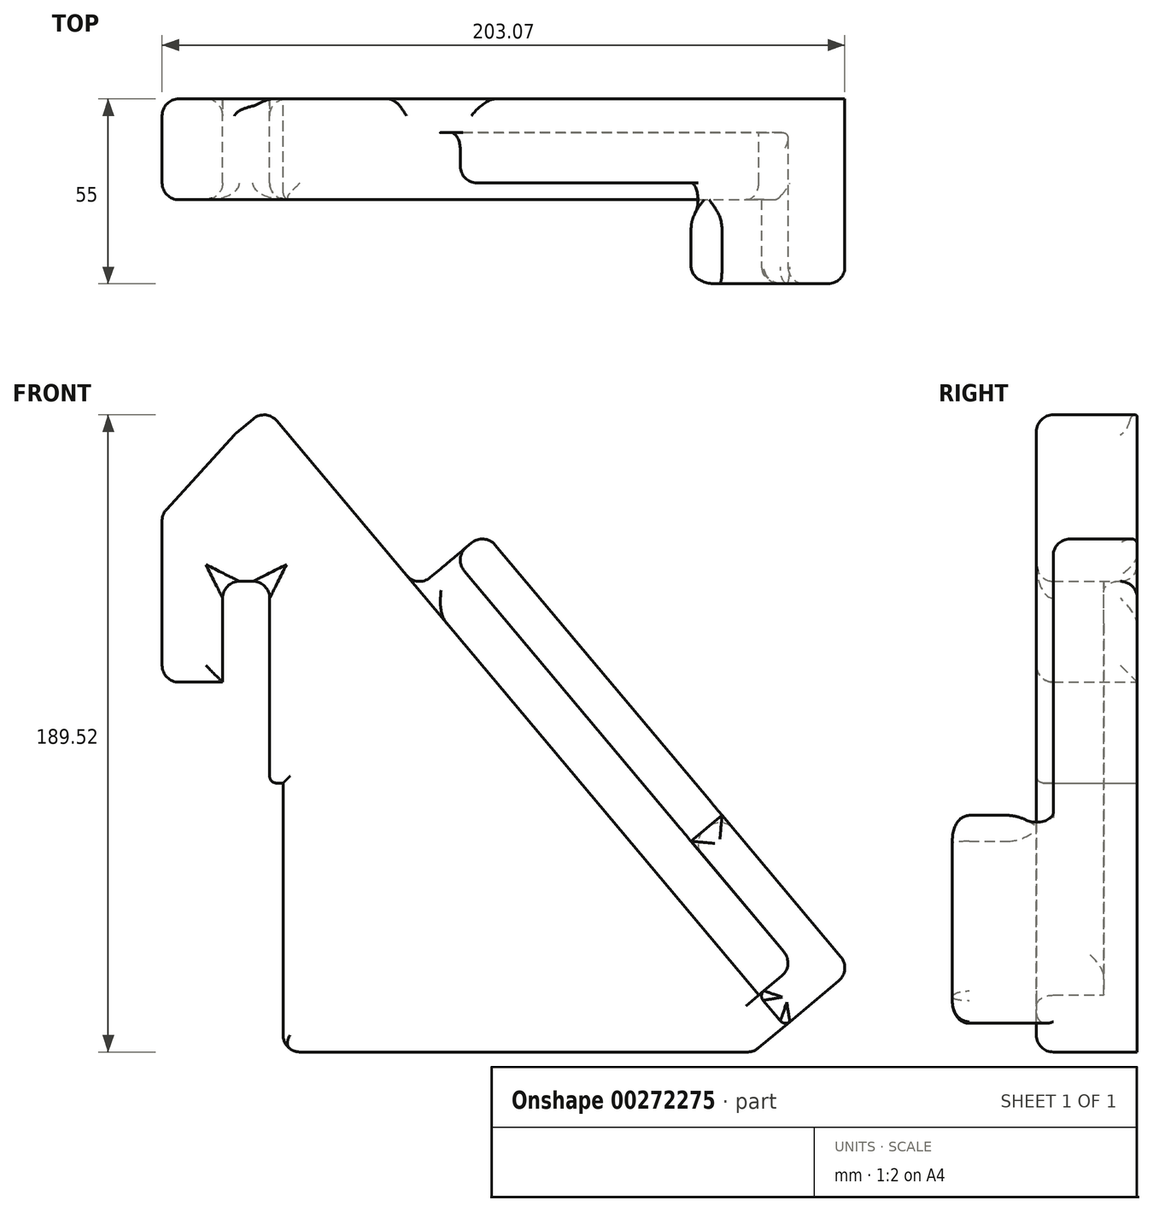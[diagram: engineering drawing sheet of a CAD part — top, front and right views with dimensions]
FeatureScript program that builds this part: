
annotation { "Feature Type Name" : "Feature", "Feature Type Description" : "" }
export const myFeature = defineFeature(function(context is Context, id is Id, definition is map)
    precondition{}
    {
        {
            var Q0;
            Q0=qCreatedBy(makeId("Front.planeOp"),FACE);
            var sketch = newSketch(context, id + "F0", { "sketchPlane" : qUnion([Q0])});
            skLineSegment(sketch, "E0", {"start": v(0, 0) * mm, "end": v(0, 50) * mm});
            skLineSegment(sketch, "E1", {"start": v(0, 50) * mm, "end": v(41.74, 50) * mm});
            skLineSegment(sketch, "E2", {"start": v(41.74, 50) * mm, "end": v(176, -110) * mm});
            skLineSegment(sketch, "E3", {"start": v(176, -110) * mm, "end": v(205.1, -85.57) * mm});
            skLineSegment(sketch, "E4", {"start": v(205.1, -85.57) * mm, "end": v(166.54, -39.61) * mm});
            skLineSegment(sketch, "E5", {"start": v(32, 0) * mm, "end": v(32, -30) * mm});
            skLineSegment(sketch, "E6", {"start": v(32, -30) * mm, "end": v(36, -30) * mm});
            skLineSegment(sketch, "E7", {"start": v(36, -30) * mm, "end": v(36, -110) * mm});
            skLineSegment(sketch, "E8", {"start": v(36, -110) * mm, "end": v(176, -110) * mm});
            skLineSegment(sketch, "E9", {"start": v(32, 0) * mm, "end": v(32, 0) * mm});
            skLineSegment(sketch, "E10", {"start": v(0, 0) * mm, "end": v(18, 0) * mm});
            skLineSegment(sketch, "E11", {"start": v(18, 0) * mm, "end": v(18, 30) * mm});
            skLineSegment(sketch, "E12", {"start": v(18, 30) * mm, "end": v(32, 30) * mm});
            skLineSegment(sketch, "E13", {"start": v(32, 30) * mm, "end": v(32, 0) * mm});
            skLineSegment(sketch, "E14", {"start": v(41.74, 50) * mm, "end": v(21.73, 73.85) * mm});
            skLineSegment(sketch, "E15", {"start": v(21.73, 73.85) * mm, "end": v(30.92, 81.56) * mm});
            skLineSegment(sketch, "E16", {"start": v(30.92, 81.56) * mm, "end": v(177.48, -93.1) * mm});
            skLineSegment(sketch, "E17", {"start": v(177.48, -93.1) * mm, "end": v(188.2, -84.1) * mm});
            skLineSegment(sketch, "E18", {"start": v(188.2, -84.1) * mm, "end": v(157.35, -47.32) * mm});
            skLineSegment(sketch, "E19", {"start": v(157.35, -47.32) * mm, "end": v(166.54, -39.61) * mm});
            skLineSegment(sketch, "E20", {"start": v(0, 50) * mm, "end": v(21.73, 73.85) * mm});
            skSolve(sketch);
        }
        {
            var Q0;
            Q0=makeQuery(id+"F0.imprint","IMPRINT",FACE,{"disambiguationData":[TD([[makeQuery(id+"F0.imprint","IMPRINT",EDGE,{"derivedFrom":sQuery(id+"F0.wireOp",EDGE,"E0")}),-1.0]])]});
            var Q1;
            Q1=makeQuery(id+"F0.imprint","IMPRINT",FACE,{"disambiguationData":[TD([[makeQuery(id+"F0.imprint","IMPRINT",EDGE,{"derivedFrom":sQuery(id+"F0.wireOp",EDGE,"E2")}),1.0]])]});
            var Q2;
            Q2=makeQuery(id+"F0.imprint","IMPRINT",FACE,{"disambiguationData":[TD([[makeQuery(id+"F0.imprint","IMPRINT",EDGE,{"derivedFrom":sQuery(id+"F0.wireOp",EDGE,"E1")}),1.0]])]});
            extrude(context, id + "F1", {"entities" : qUnion([Q0, Q1, Q2]), "depth" : 30 * mm});
        }
        {
            var Q0;
            Q0=makeQuery(id+"F1.opExtrude","CAP_FACE",FACE,{"disambiguationData":[OSD([sQuery(id+"F0.wireOp",EDGE,"E0"),sQuery(id+"F0.wireOp",EDGE,"E1"),sQuery(id+"F0.wireOp",EDGE,"E3"),sQuery(id+"F0.wireOp",EDGE,"E4"),sQuery(id+"F0.wireOp",EDGE,"E5"),sQuery(id+"F0.wireOp",EDGE,"E6"),sQuery(id+"F0.wireOp",EDGE,"E7"),sQuery(id+"F0.wireOp",EDGE,"E8"),sQuery(id+"F0.wireOp",EDGE,"E10"),sQuery(id+"F0.wireOp",EDGE,"E11"),sQuery(id+"F0.wireOp",EDGE,"E12"),sQuery(id+"F0.wireOp",EDGE,"E13"),sQuery(id+"F0.wireOp",EDGE,"E14"),sQuery(id+"F0.wireOp",EDGE,"E15"),sQuery(id+"F0.wireOp",EDGE,"E16"),sQuery(id+"F0.wireOp",EDGE,"E17"),sQuery(id+"F0.wireOp",EDGE,"E18"),sQuery(id+"F0.wireOp",EDGE,"E19")])],"isStart":true});
            var sketch = newSketch(context, id + "F2", { "sketchPlane" : qUnion([Q0])});
            skLineSegment(sketch, "E21", {"start": v(-188.2, -84.1) * mm, "end": v(-177.48, -93.1) * mm});
            skLineSegment(sketch, "E22", {"start": v(-188.2, -84.1) * mm, "end": v(-157.35, -47.32) * mm});
            skLineSegment(sketch, "E23", {"start": v(-157.35, -47.32) * mm, "end": v(-146.63, -56.32) * mm});
            skLineSegment(sketch, "E24", {"start": v(-146.63, -56.32) * mm, "end": v(-177.48, -93.1) * mm});
            skSolve(sketch);
        }
        {
            var Q0;
            Q0=makeQuery(id+"F2.imprint","IMPRINT",FACE,{"disambiguationData":[TD([[makeQuery(id+"F2.imprint","IMPRINT",EDGE,{"derivedFrom":sQuery(id+"F2.wireOp",EDGE,"E21")}),-1.0]])]});
            extrude(context, id + "F3", {"entities" : qUnion([Q0]), "operationType" : NewBodyOperationType.ADD, "oppositeDirection" : true, "depth" : 10 * mm});
        }
        {
            var Q0;
            Q0=makeQuery(id+"F1.opExtrude","CAP_FACE",FACE,{"disambiguationData":[OSD([sQuery(id+"F0.wireOp",EDGE,"E0"),sQuery(id+"F0.wireOp",EDGE,"E1"),sQuery(id+"F0.wireOp",EDGE,"E3"),sQuery(id+"F0.wireOp",EDGE,"E4"),sQuery(id+"F0.wireOp",EDGE,"E5"),sQuery(id+"F0.wireOp",EDGE,"E6"),sQuery(id+"F0.wireOp",EDGE,"E7"),sQuery(id+"F0.wireOp",EDGE,"E8"),sQuery(id+"F0.wireOp",EDGE,"E10"),sQuery(id+"F0.wireOp",EDGE,"E11"),sQuery(id+"F0.wireOp",EDGE,"E12"),sQuery(id+"F0.wireOp",EDGE,"E13"),sQuery(id+"F0.wireOp",EDGE,"E14"),sQuery(id+"F0.wireOp",EDGE,"E15"),sQuery(id+"F0.wireOp",EDGE,"E16"),sQuery(id+"F0.wireOp",EDGE,"E17"),sQuery(id+"F0.wireOp",EDGE,"E18"),sQuery(id+"F0.wireOp",EDGE,"E19")])],"isStart":false});
            var sketch = newSketch(context, id + "F4", { "sketchPlane" : qUnion([Q0])});
            skLineSegment(sketch, "E25", {"start": v(177.48, -93.1) * mm, "end": v(185.2, -102.29) * mm});
            skLineSegment(sketch, "E26", {"start": v(185.2, -102.29) * mm, "end": v(205.1, -85.57) * mm});
            skLineSegment(sketch, "E27", {"start": v(205.1, -85.57) * mm, "end": v(166.54, -39.61) * mm});
            skLineSegment(sketch, "E28", {"start": v(166.54, -39.61) * mm, "end": v(157.35, -47.32) * mm});
            skLineSegment(sketch, "E29", {"start": v(157.35, -47.32) * mm, "end": v(188.2, -84.1) * mm});
            skLineSegment(sketch, "E30", {"start": v(188.2, -84.1) * mm, "end": v(177.48, -93.1) * mm});
            skSolve(sketch);
        }
        {
            var Q0;
            Q0=makeQuery(id+"F4.imprint","IMPRINT",FACE,{"disambiguationData":[TD([[makeQuery(id+"F4.imprint","IMPRINT",EDGE,{"derivedFrom":sQuery(id+"F4.wireOp",EDGE,"E25")}),1.0]])]});
            extrude(context, id + "F5", {"entities" : qUnion([Q0]), "operationType" : NewBodyOperationType.ADD, "depth" : 25 * mm});
        }
        {
            var Q0;
            Q0=makeQuery(id+"F5.boolean.opBoolean","MERGE",FACE,{"derivedFrom":[makeQuery(id+"F3.boolean.opBoolean","MERGE",FACE,{"derivedFrom":[makeQuery(id+"F1.opExtrude","SWEPT_FACE",FACE,{"disambiguationData":[OSD([sQuery(id+"F0.wireOp",EDGE,"E19")])]}),makeQuery(id+"F3.opExtrude","SWEPT_FACE",FACE,{"disambiguationData":[OSD([sQuery(id+"F2.wireOp",EDGE,"E23")])]})]}),makeQuery(id+"F5.opExtrude","SWEPT_FACE",FACE,{"disambiguationData":[OSD([sQuery(id+"F4.wireOp",EDGE,"E28")])]})]});
            var sketch = newSketch(context, id + "F6", { "sketchPlane" : qUnion([Q0])});
            skLineSegment(sketch, "E31", {"start": v(76.12, -10) * mm, "end": v(90.12, -10) * mm});
            skLineSegment(sketch, "E32", {"start": v(90.12, -10) * mm, "end": v(90.12, -25) * mm});
            skLineSegment(sketch, "E33", {"start": v(90.12, -25) * mm, "end": v(102.12, -25) * mm});
            skLineSegment(sketch, "E34", {"start": v(102.12, -25) * mm, "end": v(102.12, 0) * mm});
            skLineSegment(sketch, "E35", {"start": v(102.12, 0) * mm, "end": v(76.12, 0) * mm});
            skLineSegment(sketch, "E36", {"start": v(76.12, 0) * mm, "end": v(76.12, -10) * mm});
            skSolve(sketch);
        }
        {
            var Q0;
            Q0=makeQuery(id+"F6.imprint","IMPRINT",FACE,{"disambiguationData":[TD([[makeQuery(id+"F6.imprint","IMPRINT",EDGE,{"derivedFrom":sQuery(id+"F6.wireOp",EDGE,"E31")}),-1.0]])]});
            extrude(context, id + "F7", {"entities" : qUnion([Q0]), "operationType" : NewBodyOperationType.ADD, "depth" : 110 * mm});
        }
        {
            var Q0;
            Q0=makeQuery(id+"F1.opExtrude","SWEPT_EDGE",EDGE,{"disambiguationData":[OSD([sQuery(id+"F0.wireOp",EDGE,"E14"),sQuery(id+"F0.wireOp",EDGE,"E15"),sQuery(id+"F0.wireOp",EDGE,"E20")])]});
            var Q1;
            Q1=makeQuery(id+"F1.opExtrude","SWEPT_FACE",FACE,{"disambiguationData":[OSD([sQuery(id+"F0.wireOp",EDGE,"E0")])]});
            var Q2;
            Q2=makeQuery(id+"F1.opExtrude","SWEPT_FACE",FACE,{"disambiguationData":[OSD([sQuery(id+"F0.wireOp",EDGE,"E20")])]});
            var Q3;
            Q3=makeQuery(id+"F1.opExtrude","SWEPT_EDGE",EDGE,{"disambiguationData":[OSD([sQuery(id+"F0.wireOp",EDGE,"E15"),sQuery(id+"F0.wireOp",EDGE,"E16")])]});
            var Q4;
            Q4=makeQuery(id+"F1.opExtrude","CAP_EDGE",EDGE,{"disambiguationData":[OSD([sQuery(id+"F0.wireOp",EDGE,"E16")])],"isStart":false});
            var Q5;
            Q5=makeQuery(id+"F1.opExtrude","CAP_EDGE",EDGE,{"disambiguationData":[OSD([sQuery(id+"F0.wireOp",EDGE,"E15")])],"isStart":false});
            var Q6;
            Q6=makeQuery(id+"F7.opExtrude","SWEPT_FACE",FACE,{"disambiguationData":[OSD([sQuery(id+"F6.wireOp",EDGE,"E33")])]});
            var Q7;
            Q7=makeQuery(id+"F5.opExtrude","CAP_FACE",FACE,{"disambiguationData":[OSD([sQuery(id+"F4.wireOp",EDGE,"E25"),sQuery(id+"F4.wireOp",EDGE,"E26"),sQuery(id+"F4.wireOp",EDGE,"E27"),sQuery(id+"F4.wireOp",EDGE,"E28"),sQuery(id+"F4.wireOp",EDGE,"E29"),sQuery(id+"F4.wireOp",EDGE,"E30")])],"isStart":false});
            var Q8;
            Q8=makeQuery(id+"F7.opExtrude","CAP_FACE",FACE,{"disambiguationData":[OSD([sQuery(id+"F6.wireOp",EDGE,"E31"),sQuery(id+"F6.wireOp",EDGE,"E32"),sQuery(id+"F6.wireOp",EDGE,"E33"),sQuery(id+"F6.wireOp",EDGE,"E34"),sQuery(id+"F6.wireOp",EDGE,"E35"),sQuery(id+"F6.wireOp",EDGE,"E36")])],"isStart":false});
            var Q9;
            Q9=makeQuery(id+"F7.boolean.opBoolean","MERGE",EDGE,{"derivedFrom":[makeQuery(id+"F3.opExtrude","CAP_EDGE",EDGE,{"disambiguationData":[OSD([sQuery(id+"F2.wireOp",EDGE,"E22")])],"isStart":false}),makeQuery(id+"F7.opExtrude","SWEPT_EDGE",EDGE,{"disambiguationData":[OSD([sQuery(id+"F6.wireOp",EDGE,"E31"),sQuery(id+"F6.wireOp",EDGE,"E32")])]})]});
            var Q10;
            Q10=makeQuery(id+"F5.boolean.opBoolean","MERGE",EDGE,{"derivedFrom":[makeQuery(id+"F1.opExtrude","SWEPT_EDGE",EDGE,{"disambiguationData":[OSD([sQuery(id+"F0.wireOp",EDGE,"E17"),sQuery(id+"F0.wireOp",EDGE,"E18")])]}),makeQuery(id+"F5.opExtrude","SWEPT_EDGE",EDGE,{"disambiguationData":[OSD([sQuery(id+"F4.wireOp",EDGE,"E29"),sQuery(id+"F4.wireOp",EDGE,"E30")])]})]});
            var Q11;
            Q11=makeQuery(id+"F5.boolean.opBoolean","MERGE",EDGE,{"derivedFrom":[makeQuery(id+"F1.opExtrude","SWEPT_EDGE",EDGE,{"disambiguationData":[OSD([sQuery(id+"F0.wireOp",EDGE,"E3"),sQuery(id+"F0.wireOp",EDGE,"E4")])]}),makeQuery(id+"F5.opExtrude","SWEPT_EDGE",EDGE,{"disambiguationData":[OSD([sQuery(id+"F4.wireOp",EDGE,"E26"),sQuery(id+"F4.wireOp",EDGE,"E27")])]})]});
            var Q12;
            Q12=makeQuery(id+"F1.opExtrude","SWEPT_EDGE",EDGE,{"disambiguationData":[OSD([sQuery(id+"F0.wireOp",EDGE,"E2"),sQuery(id+"F0.wireOp",EDGE,"E3"),sQuery(id+"F0.wireOp",EDGE,"E8")])]});
            var Q13;
            Q13=makeQuery(id+"F1.opExtrude","CAP_EDGE",EDGE,{"disambiguationData":[OSD([sQuery(id+"F0.wireOp",EDGE,"E8")])],"isStart":false});
            var Q14;
            Q14=makeQuery(id+"F1.opExtrude","CAP_EDGE",EDGE,{"disambiguationData":[OSD([sQuery(id+"F0.wireOp",EDGE,"E3")])],"isStart":false});
            var Q15;
            Q15=makeQuery(id+"F1.opExtrude","CAP_EDGE",EDGE,{"disambiguationData":[OSD([sQuery(id+"F0.wireOp",EDGE,"E5"),sQuery(id+"F0.wireOp",EDGE,"E13")])],"isStart":false});
            var Q16;
            Q16=makeQuery(id+"F1.opExtrude","CAP_EDGE",EDGE,{"disambiguationData":[OSD([sQuery(id+"F0.wireOp",EDGE,"E12")])],"isStart":false});
            var Q17;
            Q17=makeQuery(id+"F1.opExtrude","CAP_EDGE",EDGE,{"disambiguationData":[OSD([sQuery(id+"F0.wireOp",EDGE,"E11")])],"isStart":false});
            var Q18;
            Q18=makeQuery(id+"F1.opExtrude","CAP_EDGE",EDGE,{"disambiguationData":[OSD([sQuery(id+"F0.wireOp",EDGE,"E10")])],"isStart":false});
            var Q19;
            Q19=makeQuery(id+"F1.opExtrude","SWEPT_EDGE",EDGE,{"disambiguationData":[OSD([sQuery(id+"F0.wireOp",EDGE,"E7"),sQuery(id+"F0.wireOp",EDGE,"E8")])]});
            fillet(context, id + "F8", {"entities" : qUnion([Q0, Q1, Q2, Q3, Q4, Q5, Q6, Q7, Q8, Q9, Q10, Q11, Q12, Q13, Q14, Q15, Q16, Q17, Q18, Q19]), "radius" : 5 * mm, "tangentPropagation" : true, "allowEdgeOverflow" : false});
        }
        {
            var Q0;
            Q0=makeQuery(id+"F8.opFillet","BLEND_EDGE",EDGE,{"blendedFrom":[makeQuery(id+"F1.opExtrude","CAP_EDGE",EDGE,{"disambiguationData":[OSD([sQuery(id+"F0.wireOp",EDGE,"E5"),sQuery(id+"F0.wireOp",EDGE,"E13")])],"isStart":false}),makeQuery(id+"F1.opExtrude","SWEPT_FACE",FACE,{"disambiguationData":[OSD([sQuery(id+"F0.wireOp",EDGE,"E7")])]})],"blendedInto":[makeQuery(id+"F1.opExtrude","SWEPT_FACE",FACE,{"disambiguationData":[OSD([sQuery(id+"F0.wireOp",EDGE,"E7")])]})]});
            var Q1;
            Q1=makeQuery(id+"F1.opExtrude","SWEPT_EDGE",EDGE,{"disambiguationData":[OSD([sQuery(id+"F0.wireOp",EDGE,"E5"),sQuery(id+"F0.wireOp",EDGE,"E6")])]});
            var Q2;
            Q2=makeQuery(id+"F5.opExtrude","CAP_EDGE",EDGE,{"disambiguationData":[OSD([sQuery(id+"F4.wireOp",EDGE,"E25")])],"isStart":true});
            var Q3;
            Q3=makeQuery(id+"F5.opExtrude","SWEPT_EDGE",EDGE,{"disambiguationData":[OSD([sQuery(id+"F0.wireOp",EDGE,"E16"),sQuery(id+"F4.wireOp",EDGE,"E25"),sQuery(id+"F4.wireOp",EDGE,"E30")])]});
            var Q4;
            Q4=makeQuery(id+"F5.opExtrude","SWEPT_EDGE",EDGE,{"disambiguationData":[OSD([sQuery(id+"F0.wireOp",EDGE,"E3"),sQuery(id+"F4.wireOp",EDGE,"E25"),sQuery(id+"F4.wireOp",EDGE,"E26")])]});
            fillet(context, id + "F9", {"entities" : qUnion([Q0, Q1, Q2, Q3, Q4]), "radius" : 2 * mm, "tangentPropagation" : true, "allowEdgeOverflow" : false});
        }
        {
            var Q0;
            Q0=makeQuery(id+"F1.opExtrude","SWEPT_FACE",FACE,{"disambiguationData":[OSD([sQuery(id+"F0.wireOp",EDGE,"E12")])]});
            fillet(context, id + "F10", {"entities" : qUnion([Q0]), "radius" : 5 * mm, "tangentPropagation" : true, "allowEdgeOverflow" : false});
        }
    });
